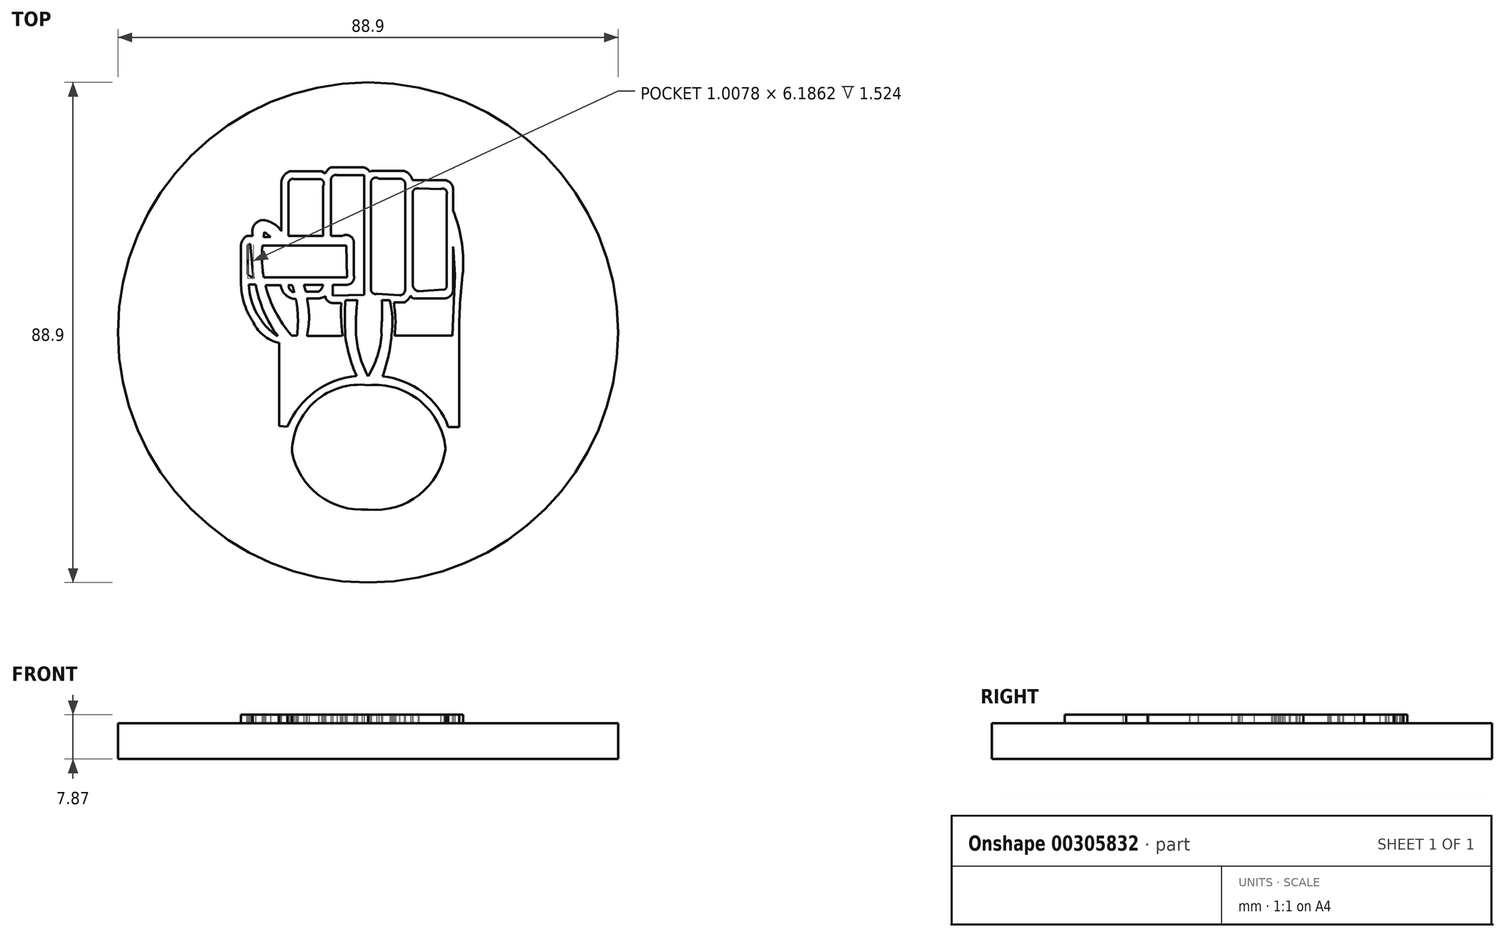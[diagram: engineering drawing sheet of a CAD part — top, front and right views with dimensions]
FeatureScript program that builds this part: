
annotation { "Feature Type Name" : "Feature", "Feature Type Description" : "" }
export const myFeature = defineFeature(function(context is Context, id is Id, definition is map)
    precondition{}
    {
        {
            var Q0;
            Q0=qCreatedBy(makeId("Top.planeOp"),FACE);
            var sketch = newSketch(context, id + "F0", { "sketchPlane" : qUnion([Q0])});
            skCircle(sketch, "E0", {"center": v(0, 0) * mm, "radius": 44.45 * mm});
            skSolve(sketch);
        }
        {
            var Q0;
            Q0 = qSketchRegion(id + "F0", true);
            extrude(context, id + "F1", {"entities" : qUnion([Q0]), "depth" : 6.35 * mm});
        }
        {
            var Q0;
            Q0=makeQuery(id+"F1.opExtrude","CAP_FACE",FACE,{"disambiguationData":[OSD([sQuery(id+"F0.wireOp",EDGE,"E0")])],"isStart":false});
            var sketch = newSketch(context, id + "F2", { "sketchPlane" : qUnion([Q0])});
            skLineSegment(sketch, "E1", {"start": v(16.17, -16.79) * mm, "end": v(16.17, -0.65) * mm});
            skLineSegment(sketch, "E2", {"start": v(16.17, -16.79) * mm, "end": v(14.27, -16.79) * mm});
            skArc(sketch, "E3", {"start": v(14.27, -16.79) * mm, "mid": v(9.71, -10.6) * mm, "end": v(2.56, -7.82) * mm});
            skArc(sketch, "E4", {"start": v(2.56, -7.82) * mm, "mid": v(3.62, -4.24) * mm, "end": v(4.15, -0.54) * mm});
            skPoint(sketch, "E5.endSnap0", {"position": v(2.45, 5.73) * mm});
            skArc(sketch, "E6", {"start": v(-2.04, -7.73) * mm, "mid": v(-9.43, -10.52) * mm, "end": v(-14.31, -16.72) * mm});
            skArc(sketch, "E7", {"start": v(2.33, 0) * mm, "mid": v(2.48, 2.86) * mm, "end": v(2.45, 5.73) * mm});
            skArc(sketch, "E8", {"start": v(-1.9, 5.73) * mm, "mid": v(-2.13, 2.87) * mm, "end": v(-2.16, 0) * mm});
            skLineSegment(sketch, "E9", {"start": v(2.4, -0.36) * mm, "end": v(2.33, 0) * mm});
            skLineSegment(sketch, "E10", {"start": v(-2.14, -0.36) * mm, "end": v(-2.16, 0) * mm});
            skLineSegment(sketch, "E11", {"start": v(-1.9, 5.73) * mm, "end": v(-4, 5.73) * mm});
            skArc(sketch, "E12", {"start": v(-4, 5.73) * mm, "mid": v(-4.04, 5.5) * mm, "end": v(-4.07, 5.25) * mm});
            skLineSegment(sketch, "E13", {"start": v(2.45, 5.73) * mm, "end": v(3.88, 5.73) * mm});
            skArc(sketch, "E14", {"start": v(-2.14, -0.36) * mm, "mid": v(-1.47, -4.18) * mm, "end": v(0, -7.77) * mm});
            skArc(sketch, "E15", {"start": v(0, -7.77) * mm, "mid": v(1.65, -4.21) * mm, "end": v(2.4, -0.36) * mm});
            skArc(sketch, "E16", {"start": v(16.89, 10.89) * mm, "mid": v(16.35, 5.13) * mm, "end": v(16.17, -0.65) * mm});
            skArc(sketch, "E17", {"start": v(16.89, 10.89) * mm, "mid": v(16.6, 16.38) * mm, "end": v(15.11, 21.68) * mm});
            skLineSegment(sketch, "E18", {"start": v(15.11, 21.68) * mm, "end": v(15.11, 25.47) * mm});
            skArc(sketch, "E19", {"start": v(15.11, 25.47) * mm, "mid": v(14.7, 26.54) * mm, "end": v(13.68, 27.06) * mm});
            skLineSegment(sketch, "E20", {"start": v(13.68, 27.06) * mm, "end": v(7.9, 27.06) * mm});
            skArc(sketch, "E21", {"start": v(7.9, 27.06) * mm, "mid": v(7.37, 28.09) * mm, "end": v(6.4, 28.7) * mm});
            skLineSegment(sketch, "E22", {"start": v(6.4, 28.7) * mm, "end": v(0.55, 28.7) * mm});
            skLineSegment(sketch, "E23", {"start": v(0.55, 28.7) * mm, "end": v(0.34, 28.52) * mm});
            skArc(sketch, "E24", {"start": v(0.34, 28.52) * mm, "mid": v(-0.26, 29.13) * mm, "end": v(-1.08, 29.39) * mm});
            skLineSegment(sketch, "E25", {"start": v(-1.08, 29.39) * mm, "end": v(-6.6, 29.39) * mm});
            skArc(sketch, "E26", {"start": v(-6.6, 29.39) * mm, "mid": v(-7.17, 28.89) * mm, "end": v(-7.6, 28.26) * mm});
            skLineSegment(sketch, "E27", {"start": v(-7.6, 28.26) * mm, "end": v(-8.28, 28.63) * mm});
            skLineSegment(sketch, "E28", {"start": v(-8.28, 28.63) * mm, "end": v(-13.9, 28.63) * mm});
            skArc(sketch, "E29", {"start": v(-13.9, 28.63) * mm, "mid": v(-14.91, 27.94) * mm, "end": v(-15.4, 26.81) * mm});
            skLineSegment(sketch, "E30", {"start": v(-15.4, 26.81) * mm, "end": v(-15.4, 18) * mm});
            skArc(sketch, "E31", {"start": v(-15.4, 18) * mm, "mid": v(-16.88, 19.4) * mm, "end": v(-18.83, 20.02) * mm});
            skArc(sketch, "E32", {"start": v(-18.83, 20.02) * mm, "mid": v(-20.29, 18.98) * mm, "end": v(-20.48, 17.2) * mm});
            skLineSegment(sketch, "E33", {"start": v(-20.48, 17.2) * mm, "end": v(-21.57, 17.2) * mm});
            skArc(sketch, "E34", {"start": v(-21.57, 17.2) * mm, "mid": v(-22.22, 16.53) * mm, "end": v(-22.6, 15.68) * mm});
            skLineSegment(sketch, "E35", {"start": v(-22.6, 8.92) * mm, "end": v(-22.6, 15.68) * mm});
            skArc(sketch, "E36", {"start": v(-22.6, 8.92) * mm, "mid": v(-22.08, 5.37) * mm, "end": v(-20.57, 2.12) * mm});
            skArc(sketch, "E37", {"start": v(-20.57, 2.12) * mm, "mid": v(-18.67, -0.44) * mm, "end": v(-15.82, -1.85) * mm});
            skLineSegment(sketch, "E38", {"start": v(-15.82, -1.85) * mm, "end": v(-15.82, -16.6) * mm});
            skLineSegment(sketch, "E39", {"start": v(-15.82, -16.6) * mm, "end": v(-14.31, -16.72) * mm});
            skArc(sketch, "E40", {"start": v(0, -9.37) * mm, "mid": v(-9.4, -12.25) * mm, "end": v(-13.52, -21.19) * mm});
            skArc(sketch, "E41", {"start": v(13.77, -20.6) * mm, "mid": v(9.21, -12.13) * mm, "end": v(0, -9.37) * mm});
            skArc(sketch, "E42", {"start": v(0, -31.45) * mm, "mid": v(9.1, -28.84) * mm, "end": v(13.77, -20.6) * mm});
            skArc(sketch, "E43", {"start": v(-13.52, -21.19) * mm, "mid": v(-8.74, -28.93) * mm, "end": v(0, -31.45) * mm});
            skArc(sketch, "E44", {"start": v(-14.31, -16.72) * mm, "mid": v(-11.54, -28.55) * mm, "end": v(0, -32.35) * mm});
            skArc(sketch, "E45", {"start": v(0, -32.35) * mm, "mid": v(11.52, -28.6) * mm, "end": v(14.27, -16.79) * mm});
            skLineSegment(sketch, "E46", {"start": v(15.11, 21.68) * mm, "end": v(15.11, 7.63) * mm});
            skArc(sketch, "E47", {"start": v(13.5, 6.05) * mm, "mid": v(14.63, 6.5) * mm, "end": v(15.11, 7.63) * mm});
            skLineSegment(sketch, "E48", {"start": v(13.5, 6.05) * mm, "end": v(8.23, 6.05) * mm});
            skArc(sketch, "E49", {"start": v(7.59, 6.56) * mm, "mid": v(7.82, 6.2) * mm, "end": v(8.23, 6.05) * mm});
            skArc(sketch, "E50", {"start": v(6.5, 5.38) * mm, "mid": v(7.13, 5.9) * mm, "end": v(7.59, 6.56) * mm});
            skLineSegment(sketch, "E51", {"start": v(6.5, 5.38) * mm, "end": v(4.55, 5.38) * mm});
            skLineSegment(sketch, "E52", {"start": v(2.46, 5.35) * mm, "end": v(0.85, 5.35) * mm});
            skArc(sketch, "E53", {"start": v(0, 5.85) * mm, "mid": v(0.36, 5.48) * mm, "end": v(0.85, 5.35) * mm});
            skArc(sketch, "E54", {"start": v(-1.13, 5.35) * mm, "mid": v(-0.51, 5.48) * mm, "end": v(0, 5.85) * mm});
            skLineSegment(sketch, "E55", {"start": v(-1.13, 5.35) * mm, "end": v(-1.94, 5.35) * mm});
            skLineSegment(sketch, "E56", {"start": v(-4.76, 5.25) * mm, "end": v(-6.3, 5.25) * mm});
            skArc(sketch, "E57", {"start": v(-7.58, 6.44) * mm, "mid": v(-7.17, 5.6) * mm, "end": v(-6.3, 5.25) * mm});
            skArc(sketch, "E58", {"start": v(-8.8, 6.06) * mm, "mid": v(-8.17, 6.19) * mm, "end": v(-7.58, 6.44) * mm});
            skLineSegment(sketch, "E59", {"start": v(-8.8, 6.06) * mm, "end": v(-10.88, 6.06) * mm});
            skArc(sketch, "E60", {"start": v(-10.88, -0.63) * mm, "mid": v(-10.48, 2.71) * mm, "end": v(-10.88, 6.06) * mm});
            skLineSegment(sketch, "E61", {"start": v(-10.88, -0.63) * mm, "end": v(-4.96, -0.63) * mm});
            skLineSegment(sketch, "E62", {"start": v(14.98, -0.54) * mm, "end": v(4.7, -0.54) * mm});
            skLineSegment(sketch, "E63", {"start": v(14.98, -0.54) * mm, "end": v(15.44, 10.27) * mm});
            skLineSegment(sketch, "E64", {"start": v(15.44, 10.27) * mm, "end": v(15.11, 15.24) * mm});
            skArc(sketch, "E65", {"start": v(-21.2, 8.55) * mm, "mid": v(-19.73, 3.31) * mm, "end": v(-16.04, -0.7) * mm});
            skLineSegment(sketch, "E66", {"start": v(-21.2, 8.55) * mm, "end": v(-20.02, 8.55) * mm});
            skArc(sketch, "E67", {"start": v(-18.41, 17.88) * mm, "mid": v(-18.16, 8.1) * mm, "end": v(-13.59, -0.55) * mm});
            skLineSegment(sketch, "E68", {"start": v(-18.41, 17.88) * mm, "end": v(-17.33, 17) * mm});
            skArc(sketch, "E69", {"start": v(-12.63, -0.55) * mm, "mid": v(-12.48, 2.7) * mm, "end": v(-12.84, 5.95) * mm});
            skLineSegment(sketch, "E70", {"start": v(-13.59, -0.55) * mm, "end": v(-12.63, -0.55) * mm});
            skLineSegment(sketch, "E71", {"start": v(-15.5, 8.39) * mm, "end": v(-18.24, 8.39) * mm});
            skArc(sketch, "E72", {"start": v(-15.5, 8.39) * mm, "mid": v(-14.63, 6.67) * mm, "end": v(-12.84, 5.95) * mm});
            skLineSegment(sketch, "E73", {"start": v(-14.11, 8.5) * mm, "end": v(-13.47, 8.39) * mm});
            skArc(sketch, "E74", {"start": v(-14.11, 8.5) * mm, "mid": v(-13.88, 7.62) * mm, "end": v(-13.11, 7.15) * mm});
            skArc(sketch, "E75.trimOffspring", {"start": v(-13.11, 7.15) * mm, "mid": v(-13.28, 7.77) * mm, "end": v(-13.47, 8.39) * mm});
            skLineSegment(sketch, "E76", {"start": v(-11.04, 7.29) * mm, "end": v(-11.4, 8.5) * mm});
            skLineSegment(sketch, "E77", {"start": v(-11.4, 8.5) * mm, "end": v(-8, 8.5) * mm});
            skArc(sketch, "E78", {"start": v(-8.78, 7.29) * mm, "mid": v(-8.25, 7.8) * mm, "end": v(-8, 8.5) * mm});
            skLineSegment(sketch, "E79", {"start": v(-11.04, 7.29) * mm, "end": v(-8.78, 7.29) * mm});
            skLineSegment(sketch, "E80", {"start": v(-6.3, 8.5) * mm, "end": v(-3.77, 8.5) * mm});
            skArc(sketch, "E81", {"start": v(-3.77, 8.5) * mm, "mid": v(-2.74, 9) * mm, "end": v(-2.53, 10.14) * mm});
            skLineSegment(sketch, "E82", {"start": v(-2.53, 10.14) * mm, "end": v(-2.53, 15.98) * mm});
            skArc(sketch, "E83", {"start": v(-2.53, 15.98) * mm, "mid": v(-3.22, 17.17) * mm, "end": v(-4.6, 17.15) * mm});
            skLineSegment(sketch, "E84", {"start": v(-4.6, 17.15) * mm, "end": v(-6.6, 17.15) * mm});
            skLineSegment(sketch, "E85", {"start": v(-14.14, 17.15) * mm, "end": v(-14.14, 26.52) * mm});
            skArc(sketch, "E86", {"start": v(-13.2, 27.3) * mm, "mid": v(-13.85, 27.13) * mm, "end": v(-14.14, 26.52) * mm});
            skLineSegment(sketch, "E87", {"start": v(-13.2, 27.3) * mm, "end": v(-8.65, 27.3) * mm});
            skArc(sketch, "E88", {"start": v(-8.01, 26.03) * mm, "mid": v(-7.94, 26.86) * mm, "end": v(-8.65, 27.3) * mm});
            skLineSegment(sketch, "E89", {"start": v(-8.01, 26.03) * mm, "end": v(-8.01, 17.15) * mm});
            skLineSegment(sketch, "E90", {"start": v(-6.6, 17.15) * mm, "end": v(-6.6, 27.14) * mm});
            skLineSegment(sketch, "E91.trimOffspring", {"start": v(-8.01, 17.15) * mm, "end": v(-14.14, 17.15) * mm});
            skArc(sketch, "E92", {"start": v(-5.54, 27.98) * mm, "mid": v(-6.27, 27.81) * mm, "end": v(-6.6, 27.14) * mm});
            skLineSegment(sketch, "E93", {"start": v(-5.54, 27.98) * mm, "end": v(-0.7, 27.98) * mm});
            skLineSegment(sketch, "E94", {"start": v(-0.7, 27.98) * mm, "end": v(-0.7, 6.7) * mm});
            skLineSegment(sketch, "E95", {"start": v(-0.7, 6.7) * mm, "end": v(-6.3, 6.53) * mm});
            skLineSegment(sketch, "E96", {"start": v(-6.3, 8.5) * mm, "end": v(-6.3, 6.53) * mm});
            skLineSegment(sketch, "E97", {"start": v(0.52, 7.64) * mm, "end": v(0.52, 26.68) * mm});
            skArc(sketch, "E98", {"start": v(1.9, 27.35) * mm, "mid": v(1, 27.45) * mm, "end": v(0.52, 26.68) * mm});
            skLineSegment(sketch, "E99", {"start": v(1.9, 27.35) * mm, "end": v(5.61, 27.35) * mm});
            skArc(sketch, "E100", {"start": v(6.6, 26.12) * mm, "mid": v(6.4, 26.97) * mm, "end": v(5.61, 27.35) * mm});
            skLineSegment(sketch, "E101", {"start": v(6.6, 26.12) * mm, "end": v(6.6, 7.59) * mm});
            skArc(sketch, "E102", {"start": v(5.62, 6.61) * mm, "mid": v(6.3, 6.9) * mm, "end": v(6.6, 7.59) * mm});
            skArc(sketch, "E103", {"start": v(0.52, 7.64) * mm, "mid": v(0.85, 7) * mm, "end": v(1.55, 6.87) * mm});
            skLineSegment(sketch, "E104", {"start": v(1.55, 6.87) * mm, "end": v(5.62, 6.61) * mm});
            skLineSegment(sketch, "E105", {"start": v(7.92, 24.78) * mm, "end": v(7.92, 8.61) * mm});
            skArc(sketch, "E106", {"start": v(7.92, 8.61) * mm, "mid": v(8.2, 7.8) * mm, "end": v(8.89, 7.32) * mm});
            skArc(sketch, "E107", {"start": v(9.04, 25.6) * mm, "mid": v(8.27, 25.47) * mm, "end": v(7.92, 24.78) * mm});
            skLineSegment(sketch, "E108", {"start": v(13.96, 24.52) * mm, "end": v(13.96, 8.55) * mm});
            skLineSegment(sketch, "E109", {"start": v(13.54, 7.63) * mm, "end": v(8.89, 7.32) * mm});
            skLineSegment(sketch, "E110", {"start": v(9.04, 25.6) * mm, "end": v(12.87, 25.47) * mm});
            skArc(sketch, "E111", {"start": v(13.96, 24.52) * mm, "mid": v(13.77, 25.4) * mm, "end": v(12.87, 25.47) * mm});
            skArc(sketch, "E112", {"start": v(13.54, 7.63) * mm, "mid": v(13.94, 8) * mm, "end": v(13.96, 8.55) * mm});
            skLineSegment(sketch, "E113", {"start": v(-21.36, 15.6) * mm, "end": v(-21.36, 10.28) * mm});
            skLineSegment(sketch, "E114", {"start": v(-21.36, 10.28) * mm, "end": v(-20.35, 9.61) * mm});
            skLineSegment(sketch, "E115", {"start": v(-20.35, 9.61) * mm, "end": v(-20.95, 15.8) * mm});
            skLineSegment(sketch, "E116", {"start": v(-20.95, 15.8) * mm, "end": v(-21.36, 15.6) * mm});
            skLineSegment(sketch, "E117", {"start": v(-18.77, 15.47) * mm, "end": v(-3.9, 15.47) * mm});
            skLineSegment(sketch, "E118", {"start": v(-3.9, 15.47) * mm, "end": v(-3.77, 9.78) * mm});
            skLineSegment(sketch, "E119", {"start": v(-18.53, 9.78) * mm, "end": v(-3.77, 9.78) * mm});
            skLineSegment(sketch, "E120", {"start": v(-17.33, 17) * mm, "end": v(-18.57, 17) * mm});
            skArc(sketch, "E121", {"start": v(-20.02, 8.55) * mm, "mid": v(-18.51, 3.72) * mm, "end": v(-16.04, -0.7) * mm});
            skArc(sketch, "E122.trimOffspring", {"start": v(-4.03, -0.63) * mm, "mid": v(-3.3, -4.26) * mm, "end": v(-2.04, -7.73) * mm});
            skArc(sketch, "E123", {"start": v(-4.07, 5.25) * mm, "mid": v(-4.1, 2.3) * mm, "end": v(-4.03, -0.63) * mm});
            skArc(sketch, "E124.trimOffspring", {"start": v(3.93, 5.38) * mm, "mid": v(3.9, 5.55) * mm, "end": v(3.88, 5.73) * mm});
            skArc(sketch, "E125", {"start": v(4.7, -0.54) * mm, "mid": v(4.86, 2.42) * mm, "end": v(4.55, 5.38) * mm});
            skArc(sketch, "E126", {"start": v(4.15, -0.54) * mm, "mid": v(4.33, 2.43) * mm, "end": v(3.93, 5.38) * mm});
            skArc(sketch, "E127", {"start": v(-4.76, 5.25) * mm, "mid": v(-4.78, 2.34) * mm, "end": v(-4.5, -0.56) * mm});
            skLineSegment(sketch, "E128", {"start": v(-4.96, -0.63) * mm, "end": v(-4.5, -0.56) * mm});
            skSolve(sketch);
        }
        {
            var Q0;
            Q0=makeQuery(id+"F2.imprint","IMPRINT",FACE,{"disambiguationData":[TD([[makeQuery(id+"F2.imprint","IMPRINT",EDGE,{"derivedFrom":sQuery(id+"F2.wireOp",EDGE,"E1")}),1.0]])]});
            var Q1;
            {var subQ20=sQuery(id+"F2.wireOp",EDGE,"E6");Q1=makeQuery(id+"F2.imprint","IMPRINT",FACE,{"disambiguationData":[TD([[makeQuery(id+"F2.imprint","IMPRINT",EDGE,{"derivedFrom":subQ20}),-1.0]])]});}
            var Q2;
            {var subQ0=sQuery(id+"F2.wireOp",EDGE,"E9");Q2=makeQuery(id+"F2.imprint","IMPRINT",FACE,{"disambiguationData":[TD([[makeQuery(id+"F2.imprint","IMPRINT",EDGE,{"derivedFrom":subQ0}),1.0]])]});}
            var Q3;
            Q3=makeQuery(id+"F2.imprint","IMPRINT",FACE,{"disambiguationData":[TD([[makeQuery(id+"F2.imprint","IMPRINT",EDGE,{"derivedFrom":sQuery(id+"F2.wireOp",EDGE,"E40")}),1.0]])]});
            extrude(context, id + "F3", {"entities" : qUnion([Q0, Q1, Q2, Q3]), "operationType" : NewBodyOperationType.ADD, "depth" : 1.52 * mm});
        }
    });
